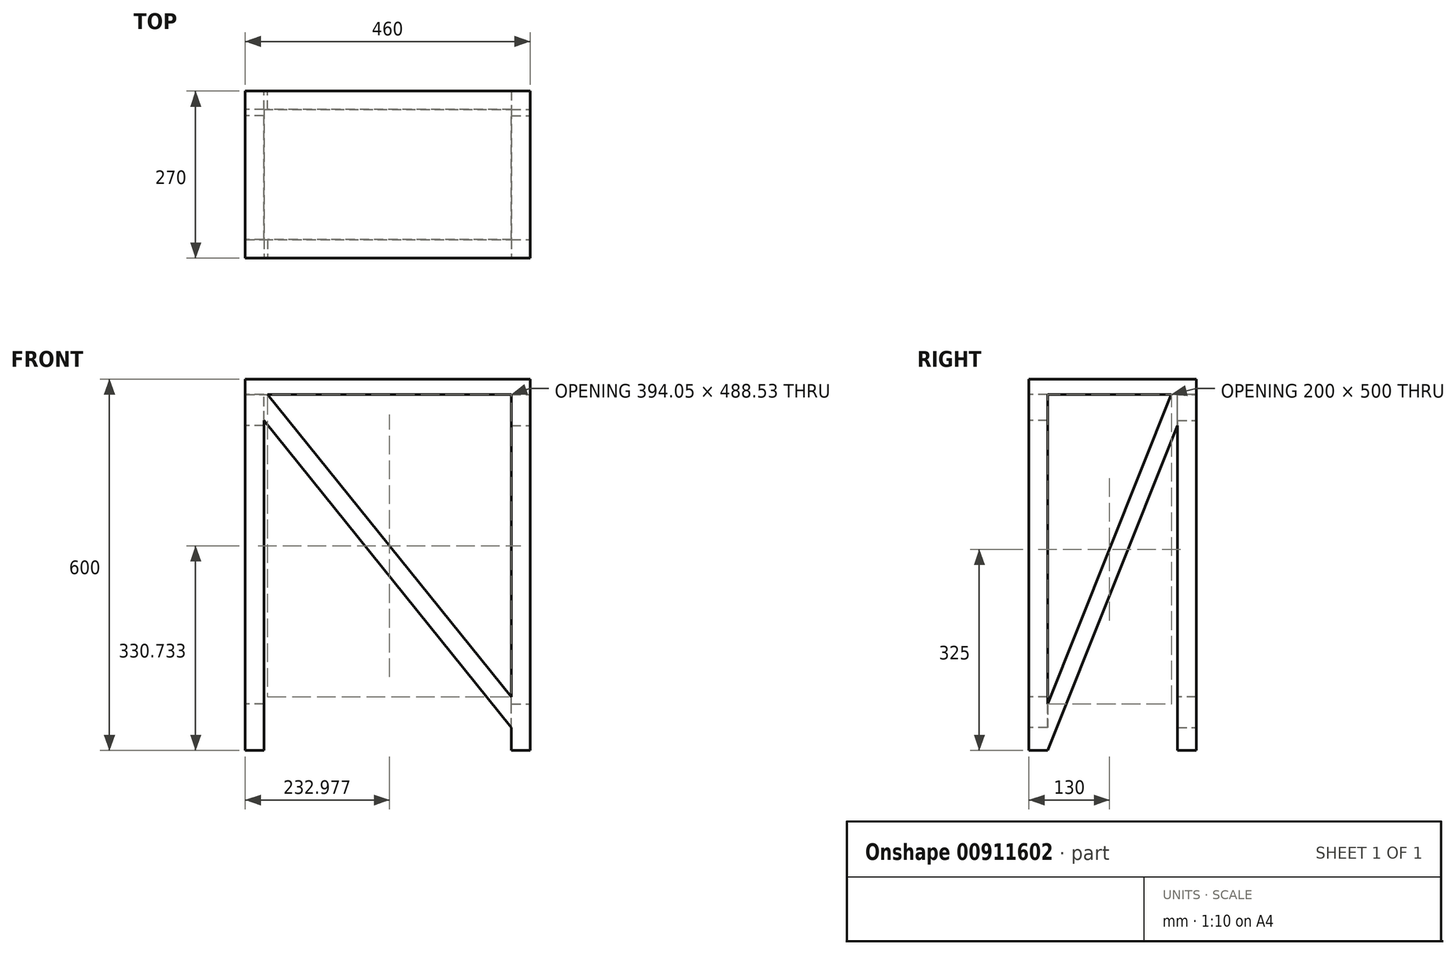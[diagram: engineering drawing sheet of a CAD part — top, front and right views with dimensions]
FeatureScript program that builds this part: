
annotation { "Feature Type Name" : "Feature", "Feature Type Description" : "" }
export const myFeature = defineFeature(function(context is Context, id is Id, definition is map)
    precondition{}
    {
        {
            var Q0;
            Q0=qCreatedBy(makeId("Top.planeOp"),FACE);
            var sketch = newSketch(context, id + "F0", { "sketchPlane" : qUnion([Q0])});
            skLineSegment(sketch, "E0.bottom", {"start": v(-200, 105) * mm, "end": v(-230, 105) * mm});
            skLineSegment(sketch, "E0.top", {"start": v(-200, 135) * mm, "end": v(-230, 135) * mm});
            skLineSegment(sketch, "E0.left", {"start": v(-200, 105) * mm, "end": v(-200, 135) * mm});
            skLineSegment(sketch, "E0.right", {"start": v(-230, 105) * mm, "end": v(-230, 135) * mm});
            skPoint(sketch, "E0.middle", {"position": v(-215, 120) * mm});
            skLineSegment(sketch, "E1.0.1.0", {"start": v(-200, -135) * mm, "end": v(-200, -105) * mm});
            skLineSegment(sketch, "E1.0.1.1", {"start": v(-230, -135) * mm, "end": v(-230, -105) * mm});
            skLineSegment(sketch, "E1.0.1.2", {"start": v(-200, -135) * mm, "end": v(-230, -135) * mm});
            skLineSegment(sketch, "E1.0.1.3", {"start": v(-200, -105) * mm, "end": v(-230, -105) * mm});
            skPoint(sketch, "E1.0.1.4", {"position": v(-215, -120) * mm});
            skLineSegment(sketch, "E1.1.0.0", {"start": v(230, 105) * mm, "end": v(230, 135) * mm});
            skLineSegment(sketch, "E1.1.0.1", {"start": v(200, 105) * mm, "end": v(200, 135) * mm});
            skLineSegment(sketch, "E1.1.0.2", {"start": v(230, 105) * mm, "end": v(200, 105) * mm});
            skLineSegment(sketch, "E1.1.0.3", {"start": v(230, 135) * mm, "end": v(200, 135) * mm});
            skPoint(sketch, "E1.1.0.4", {"position": v(215, 120) * mm});
            skLineSegment(sketch, "E1.1.1.0", {"start": v(230, -135) * mm, "end": v(230, -105) * mm});
            skLineSegment(sketch, "E1.1.1.1", {"start": v(200, -135) * mm, "end": v(200, -105) * mm});
            skLineSegment(sketch, "E1.1.1.2", {"start": v(230, -135) * mm, "end": v(200, -135) * mm});
            skLineSegment(sketch, "E1.1.1.3", {"start": v(230, -105) * mm, "end": v(200, -105) * mm});
            skPoint(sketch, "E1.1.1.4", {"position": v(215, -120) * mm});
            skLineSegment(sketch, "E1.direction1", {"start": v(-230, 105) * mm, "end": v(200, 105) * mm, "construction": true});
            skLineSegment(sketch, "E1.direction2", {"start": v(-230, 105) * mm, "end": v(-230, -135) * mm, "construction": true});
            skSolve(sketch);
        }
        {
            var Q0;
            Q0=qSketchRegion(id+"F0",true);
            extrude(context, id + "F1", {"entities" : qUnion([Q0]), "oppositeDirection" : true, "depth" : 600 * mm, "offsetDistance" : 25 * mm});
        }
        {
            var Q0;
            Q0=makeQuery(id+"F1.opExtrude","CAP_FACE",FACE,{"disambiguationData":[OSD([sQuery(id+"F0.wireOp",EDGE,"E0.bottom"),sQuery(id+"F0.wireOp",EDGE,"E0.top"),sQuery(id+"F0.wireOp",EDGE,"E0.left"),sQuery(id+"F0.wireOp",EDGE,"E0.right")])],"isStart":true});
            var sketch = newSketch(context, id + "F2", { "sketchPlane" : qUnion([Q0])});
            skLineSegment(sketch, "E2.bottom", {"start": v(-230, 135) * mm, "end": v(230, 135) * mm});
            skLineSegment(sketch, "E2.top", {"start": v(-230, -135) * mm, "end": v(230, -135) * mm});
            skLineSegment(sketch, "E2.left", {"start": v(-230, 135) * mm, "end": v(-230, -135) * mm});
            skLineSegment(sketch, "E2.right", {"start": v(230, 135) * mm, "end": v(230, -135) * mm});
            skSolve(sketch);
        }
        {
            var Q0;
            Q0=qSketchRegion(id+"F2",true);
            extrude(context, id + "F3", {"entities" : qUnion([Q0]), "operationType" : NewBodyOperationType.ADD, "oppositeDirection" : true, "depth" : 25 * mm, "offsetDistance" : 25 * mm});
        }
        {
            var Q0;
            Q0=makeQuery(id+"F3.boolean.opBoolean","MERGE",FACE,{"derivedFrom":[makeQuery(id+"F1.opExtrude","SWEPT_FACE",FACE,{"disambiguationData":[OSD([sQuery(id+"F0.wireOp",EDGE,"E1.0.1.2")])]}),makeQuery(id+"F1.opExtrude","SWEPT_FACE",FACE,{"disambiguationData":[OSD([sQuery(id+"F0.wireOp",EDGE,"E1.1.1.2")])]}),makeQuery(id+"F3.opExtrude","SWEPT_FACE",FACE,{"disambiguationData":[OSD([sQuery(id+"F2.wireOp",EDGE,"E2.top")])]})]});
            var sketch = newSketch(context, id + "F4", { "sketchPlane" : qUnion([Q0])});
            skLineSegment(sketch, "E3", {"start": v(-230, -29.7) * mm, "end": v(230, -600) * mm});
            skLineSegment(sketch, "E4", {"start": v(230, -600) * mm, "end": v(230, -550.73) * mm});
            skLineSegment(sketch, "E5", {"start": v(230, -550.73) * mm, "end": v(-214.2, 0) * mm});
            skLineSegment(sketch, "E6", {"start": v(-214.2, 0) * mm, "end": v(-230, -29.7) * mm});
            skSolve(sketch);
        }
        {
            var Q0;
            {var subQ3=sQuery(id+"F4.wireOp",EDGE,"E5");var subQ5=makeQuery(id+"F3.opExtrude","CAP_EDGE",EDGE,{"disambiguationData":[OSD([sQuery(id+"F2.wireOp",EDGE,"E2.top")])],"isStart":false});var subQ9=makeQuery(id+"F4.imprint","INTERSECT",VERTEX,{"derivedFrom":[subQ5,subQ3]});Q0=makeQuery(id+"F4.imprint","IMPRINT",FACE,{"disambiguationData":[TD([[makeQuery(id+"F4.imprint","IMPRINT",EDGE,{"disambiguationData":[TD([[subQ9,1.0]])],"derivedFrom":subQ3}),1.0]])]});}
            extrude(context, id + "F5", {"entities" : qUnion([Q0]), "operationType" : NewBodyOperationType.ADD, "oppositeDirection" : true, "depth" : 30 * mm, "offsetDistance" : 25 * mm});
        }
        {
            var Q0;
            Q0=makeQuery(id+"F1.opExtrude","SWEPT_FACE",FACE,{"disambiguationData":[OSD([sQuery(id+"F0.wireOp",EDGE,"E0.bottom")])]});
            var sketch = newSketch(context, id + "F6", { "sketchPlane" : qUnion([Q0])});
            skLineSegment(sketch, "E7.0", {"start": v(-230, -29.7) * mm, "end": v(230, -600) * mm});
            skLineSegment(sketch, "E8.0", {"start": v(230, -550.73) * mm, "end": v(-214.2, 0) * mm});
            skLineSegment(sketch, "E9.0", {"start": v(-214.2, 0) * mm, "end": v(-230, -29.7) * mm});
            skLineSegment(sketch, "E10.0", {"start": v(230, -600) * mm, "end": v(230, -550.73) * mm});
            skSolve(sketch);
        }
        {
            var Q0;
            Q0=qSketchRegion(id+"F6",true);
            extrude(context, id + "F7", {"entities" : qUnion([Q0]), "operationType" : NewBodyOperationType.ADD, "oppositeDirection" : true, "depth" : 30 * mm, "offsetDistance" : 25 * mm});
        }
        {
            var Q0;
            Q0=makeQuery(id+"F3.boolean.opBoolean","MERGE",FACE,{"derivedFrom":[makeQuery(id+"F1.opExtrude","SWEPT_FACE",FACE,{"disambiguationData":[OSD([sQuery(id+"F0.wireOp",EDGE,"E0.right")])]}),makeQuery(id+"F1.opExtrude","SWEPT_FACE",FACE,{"disambiguationData":[OSD([sQuery(id+"F0.wireOp",EDGE,"E1.0.1.1")])]}),makeQuery(id+"F3.opExtrude","SWEPT_FACE",FACE,{"disambiguationData":[OSD([sQuery(id+"F2.wireOp",EDGE,"E2.left")])]})]});
            var sketch = newSketch(context, id + "F8", { "sketchPlane" : qUnion([Q0])});
            skLineSegment(sketch, "E11", {"start": v(-135, 0) * mm, "end": v(105, -600) * mm});
            skLineSegment(sketch, "E12", {"start": v(105, -600) * mm, "end": v(135, -600) * mm});
            skLineSegment(sketch, "E13", {"start": v(135, -600) * mm, "end": v(-105, 0) * mm});
            skLineSegment(sketch, "E14", {"start": v(-105, 0) * mm, "end": v(-135, 0) * mm});
            skSolve(sketch);
        }
        {
            var Q0;
            {var subQ1=makeQuery(id+"F3.opExtrude","CAP_EDGE",EDGE,{"disambiguationData":[OSD([sQuery(id+"F2.wireOp",EDGE,"E2.left")])],"isStart":false});var subQ3=sQuery(id+"F8.wireOp",EDGE,"E13");var subQ4=makeQuery(id+"F8.imprint","INTERSECT",VERTEX,{"derivedFrom":[subQ1,subQ3]});Q0=makeQuery(id+"F8.imprint","IMPRINT",FACE,{"disambiguationData":[TD([[makeQuery(id+"F8.imprint","IMPRINT",EDGE,{"disambiguationData":[TD([[subQ4,1.0]])],"derivedFrom":subQ3}),1.0]])]});}
            extrude(context, id + "F9", {"entities" : qUnion([Q0]), "operationType" : NewBodyOperationType.ADD, "oppositeDirection" : true, "depth" : 30 * mm, "offsetDistance" : 25 * mm});
        }
        {
            var Q0;
            Q0=makeQuery(id+"F3.boolean.opBoolean","MERGE",FACE,{"derivedFrom":[makeQuery(id+"F1.opExtrude","SWEPT_FACE",FACE,{"disambiguationData":[OSD([sQuery(id+"F0.wireOp",EDGE,"E1.1.0.0")])]}),makeQuery(id+"F1.opExtrude","SWEPT_FACE",FACE,{"disambiguationData":[OSD([sQuery(id+"F0.wireOp",EDGE,"E1.1.1.0")])]}),makeQuery(id+"F3.opExtrude","SWEPT_FACE",FACE,{"disambiguationData":[OSD([sQuery(id+"F2.wireOp",EDGE,"E2.right")])]})]});
            var sketch = newSketch(context, id + "F10", { "sketchPlane" : qUnion([Q0])});
            skLineSegment(sketch, "E15.0", {"start": v(-105, -525) * mm, "end": v(95, -25) * mm});
            skLineSegment(sketch, "E16.0", {"start": v(105, -75) * mm, "end": v(-105, -600) * mm});
            skLineSegment(sketch, "E17.0", {"start": v(105, -75) * mm, "end": v(105, -25) * mm});
            skLineSegment(sketch, "E18.0", {"start": v(105, -25) * mm, "end": v(95, -25) * mm});
            skLineSegment(sketch, "E19.0", {"start": v(-105, -600) * mm, "end": v(-105, -525) * mm});
            skPoint(sketch, "E20.orphan", {"position": v(-105, -25) * mm});
            skPoint(sketch, "E21.orphan", {"position": v(105, -600) * mm});
            skSolve(sketch);
        }
        {
            var Q0;
            Q0=makeQuery(id+"F10.imprint","IMPRINT",FACE,{"disambiguationData":[TD([[makeQuery(id+"F10.imprint","IMPRINT",EDGE,{"derivedFrom":sQuery(id+"F10.wireOp",EDGE,"E15.0")}),-1.0]])]});
            extrude(context, id + "F11", {"entities" : qUnion([Q0]), "operationType" : NewBodyOperationType.ADD, "oppositeDirection" : true, "depth" : 30 * mm, "offsetDistance" : 25 * mm});
        }
    });
